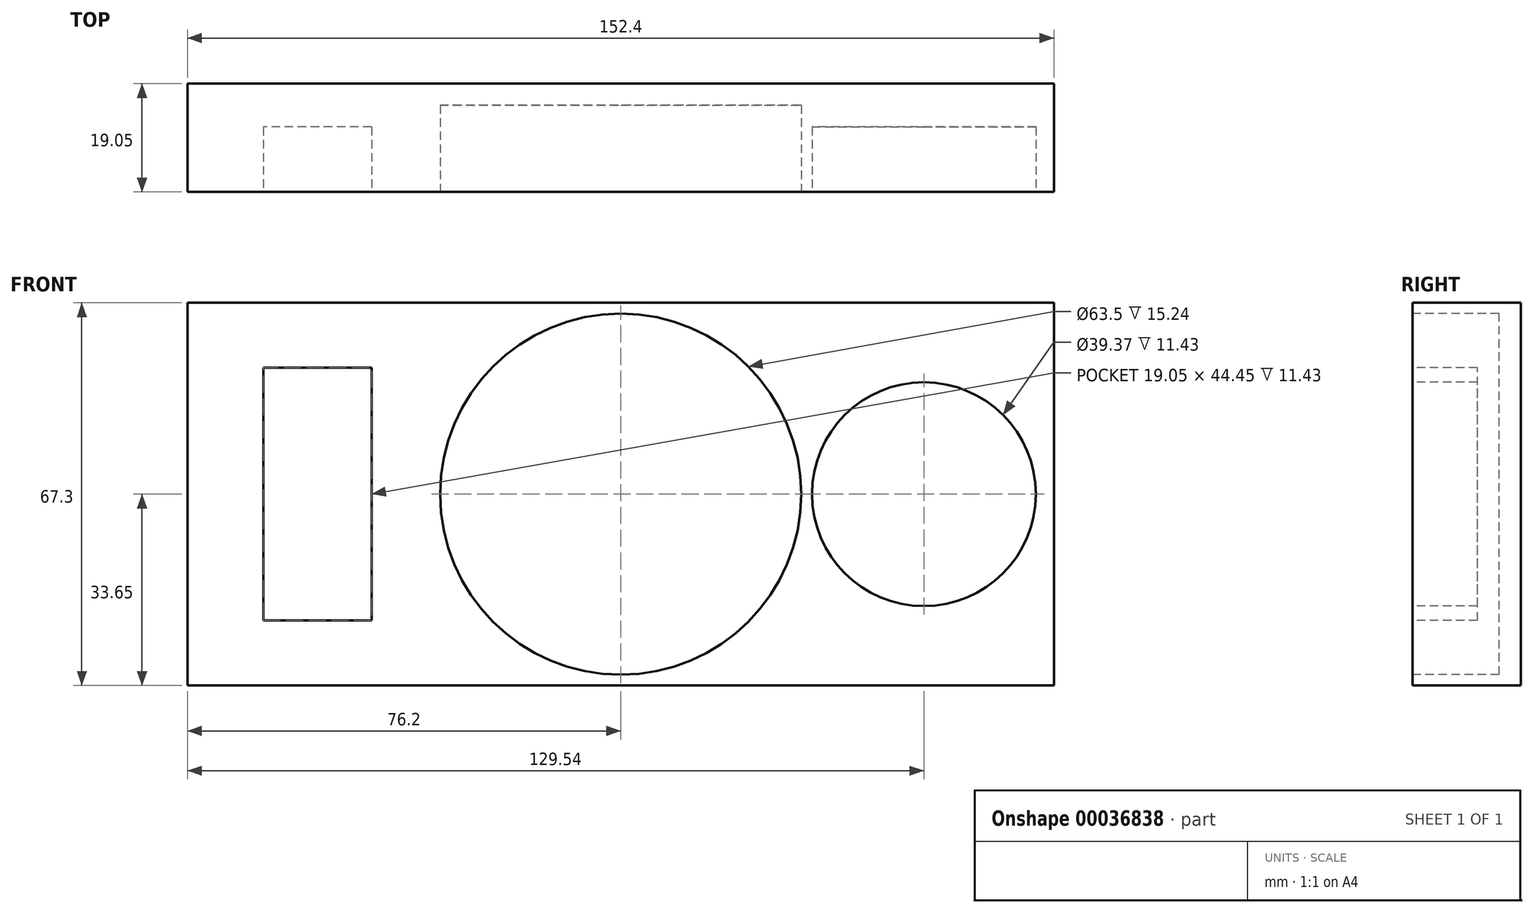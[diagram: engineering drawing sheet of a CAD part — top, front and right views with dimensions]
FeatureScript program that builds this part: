
annotation { "Feature Type Name" : "Feature", "Feature Type Description" : "" }
export const myFeature = defineFeature(function(context is Context, id is Id, definition is map)
    precondition{}
    {
        {
            var Q0;
            Q0=qCreatedBy(makeId("Front.planeOp"),FACE);
            var sketch = newSketch(context, id + "F0", { "sketchPlane" : qUnion([Q0])});
            skLineSegment(sketch, "E0.rect.bottom", {"start": v(76.2, 33.66) * mm, "end": v(-76.2, 33.66) * mm});
            skLineSegment(sketch, "E0.rect.top", {"start": v(76.2, -33.66) * mm, "end": v(-76.2, -33.66) * mm});
            skLineSegment(sketch, "E0.rect.left", {"start": v(76.2, 33.66) * mm, "end": v(76.2, -33.66) * mm});
            skLineSegment(sketch, "E0.rect.right", {"start": v(-76.2, 33.66) * mm, "end": v(-76.2, -33.66) * mm});
            skPoint(sketch, "E0.rect.middle", {"position": v(0, 0) * mm});
            skSolve(sketch);
        }
        {
            var Q0;
            Q0=makeQuery(id+"F0.imprint","IMPRINT",FACE,{"disambiguationData":[TD([[makeQuery(id+"F0.imprint","IMPRINT",EDGE,{"derivedFrom":sQuery(id+"F0.wireOp",EDGE,"E0.rect.bottom")}),1.0]])]});
            extrude(context, id + "F1", {"entities" : qUnion([Q0]), "depth" : 19.05 * mm});
        }
        {
            var Q0;
            Q0=makeQuery(id+"F1.opExtrude","CAP_FACE",FACE,{"disambiguationData":[OSD([sQuery(id+"F0.wireOp",EDGE,"E0.rect.bottom"),sQuery(id+"F0.wireOp",EDGE,"E0.rect.top"),sQuery(id+"F0.wireOp",EDGE,"E0.rect.left"),sQuery(id+"F0.wireOp",EDGE,"E0.rect.right")])],"isStart":false});
            var sketch = newSketch(context, id + "F2", { "sketchPlane" : qUnion([Q0])});
            skCircle(sketch, "E1", {"center": v(0, 0) * mm, "radius": 31.75 * mm});
            skSolve(sketch);
        }
        {
            var Q0;
            Q0 = qSketchRegion(id + "F2", true);
            extrude(context, id + "F3", {"entities" : qUnion([Q0]), "operationType" : NewBodyOperationType.REMOVE, "oppositeDirection" : true, "depth" : 15.24 * mm});
        }
        {
            var Q0;
            Q0=makeQuery(id+"F1.opExtrude","CAP_FACE",FACE,{"disambiguationData":[OSD([sQuery(id+"F0.wireOp",EDGE,"E0.rect.bottom"),sQuery(id+"F0.wireOp",EDGE,"E0.rect.top"),sQuery(id+"F0.wireOp",EDGE,"E0.rect.left"),sQuery(id+"F0.wireOp",EDGE,"E0.rect.right")])],"isStart":false});
            var sketch = newSketch(context, id + "F4", { "sketchPlane" : qUnion([Q0])});
            skCircle(sketch, "E2", {"center": v(53.34, 0) * mm, "radius": 19.69 * mm});
            skSolve(sketch);
        }
        {
            var Q0;
            Q0=makeQuery(id+"F4.imprint","IMPRINT",FACE,{"disambiguationData":[TD([[makeQuery(id+"F4.imprint","IMPRINT",EDGE,{"derivedFrom":sQuery(id+"F4.wireOp",EDGE,"E2")}),1.0]])]});
            extrude(context, id + "F5", {"entities" : qUnion([Q0]), "operationType" : NewBodyOperationType.REMOVE, "oppositeDirection" : true, "depth" : 11.43 * mm});
        }
        {
            var Q0;
            Q0=makeQuery(id+"F1.opExtrude","CAP_FACE",FACE,{"disambiguationData":[OSD([sQuery(id+"F0.wireOp",EDGE,"E0.rect.bottom"),sQuery(id+"F0.wireOp",EDGE,"E0.rect.top"),sQuery(id+"F0.wireOp",EDGE,"E0.rect.left"),sQuery(id+"F0.wireOp",EDGE,"E0.rect.right")])],"isStart":false});
            var sketch = newSketch(context, id + "F6", { "sketchPlane" : qUnion([Q0])});
            skLineSegment(sketch, "E3.rect.bottom", {"start": v(-43.82, -22.23) * mm, "end": v(-62.87, -22.23) * mm});
            skLineSegment(sketch, "E3.rect.top", {"start": v(-43.81, 22.23) * mm, "end": v(-62.87, 22.23) * mm});
            skLineSegment(sketch, "E3.rect.left", {"start": v(-43.82, -22.23) * mm, "end": v(-43.81, 22.23) * mm});
            skLineSegment(sketch, "E3.rect.right", {"start": v(-62.87, -22.23) * mm, "end": v(-62.87, 22.23) * mm});
            skPoint(sketch, "E3.rect.middle", {"position": v(-53.34, 0) * mm});
            skSolve(sketch);
        }
        {
            var Q0;
            Q0=makeQuery(id+"F6.imprint","IMPRINT",FACE,{"disambiguationData":[TD([[makeQuery(id+"F6.imprint","IMPRINT",EDGE,{"derivedFrom":sQuery(id+"F6.wireOp",EDGE,"E3.rect.bottom")}),-1.0]])]});
            extrude(context, id + "F7", {"entities" : qUnion([Q0]), "operationType" : NewBodyOperationType.REMOVE, "oppositeDirection" : true, "depth" : 11.43 * mm});
        }
    });
